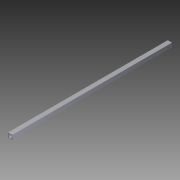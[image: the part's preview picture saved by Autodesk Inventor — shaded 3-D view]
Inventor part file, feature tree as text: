
AUTODESK INVENTOR PART (.ipt)
format: ipt  version: 2012 (Build 160160000, 160)  size: 73,728 bytes
history: native  units: in
note: dims shown in document units (in); Inventor stores cm internally (conversion verified against a paired STEP export)
features: extrude x1, sketch x1
ambient origin geometry x8: Origin, YZ Plane, XZ Plane, XY Plane, X Axis, Y Axis, Z Axis, Center Point
bodies: Solid1 (feature_tree)
feature tree (2):
  extrude  "Extrusion1"  Depth=1.0in
  sketch  "Sketch1"  dims[d0=1.0in d1=1.0in d2=0.125in d3=0.125in d4=0.125in d5=0.125in d6=37.75in d7=0.0in]
